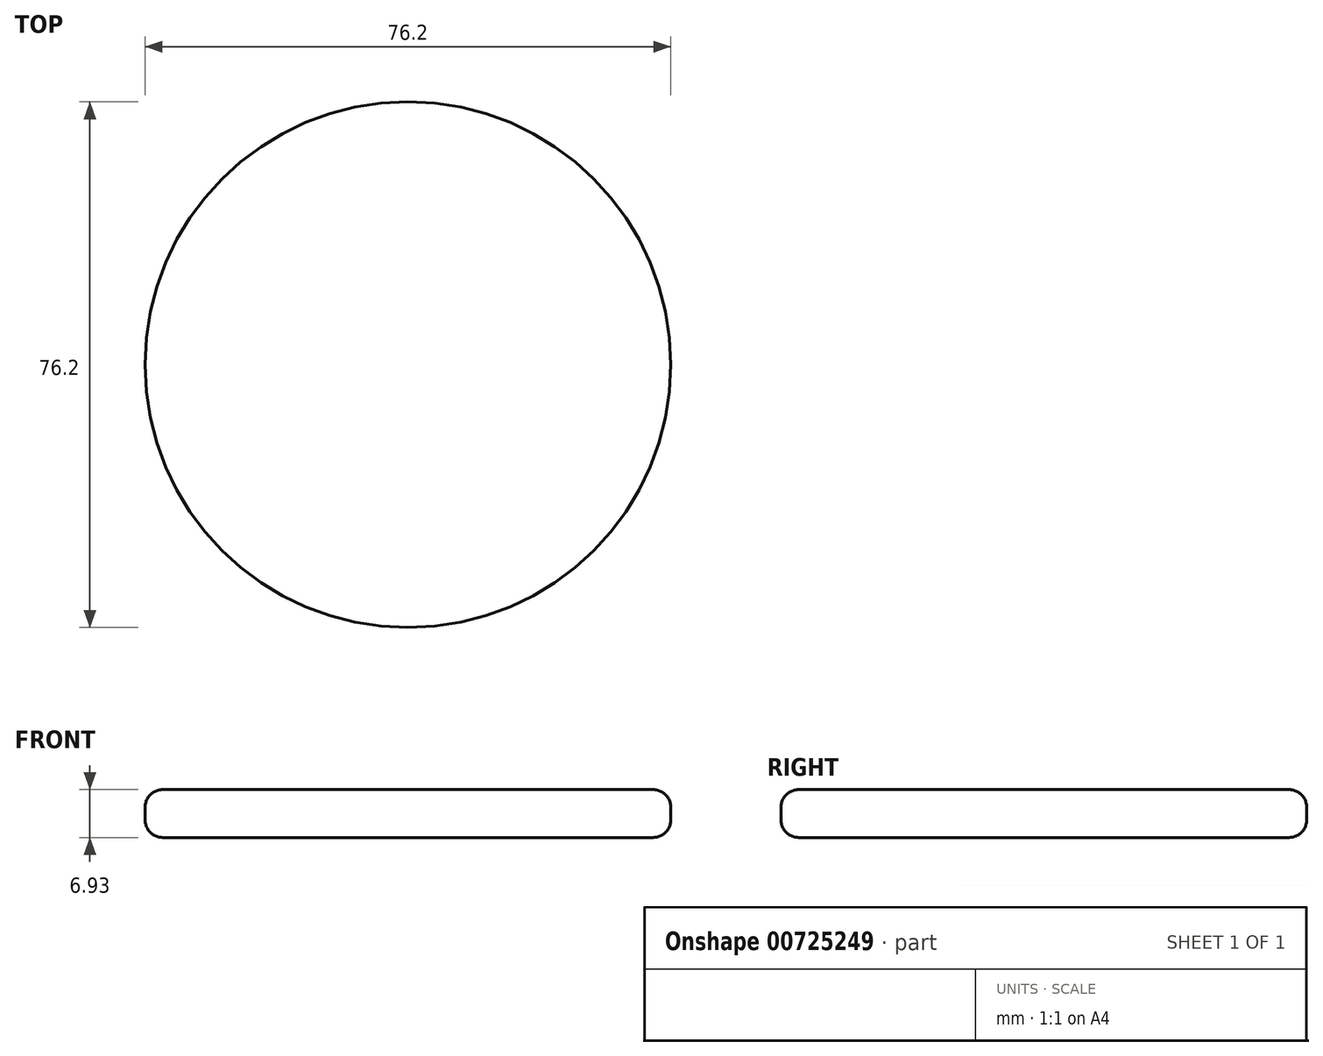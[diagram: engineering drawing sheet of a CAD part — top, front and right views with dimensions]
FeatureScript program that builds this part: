
annotation { "Feature Type Name" : "Feature", "Feature Type Description" : "" }
export const myFeature = defineFeature(function(context is Context, id is Id, definition is map)
    precondition{}
    {
        {
            var Q0;
            Q0=qCreatedBy(makeId("Top.planeOp"),FACE);
            var sketch = newSketch(context, id + "F0", { "sketchPlane" : qUnion([Q0])});
            skCircle(sketch, "E0", {"center": v(0, 0) * mm, "radius": 38.1 * mm});
            skSolve(sketch);
        }
        {
            var Q0;
            Q0 = qSketchRegion(id + "F0", true);
            extrude(context, id + "F1", {"entities" : qUnion([Q0]), "depth" : 6.93 * mm, "offsetDistance" : 25.4 * mm});
        }
        {
            var Q0;
            Q0=makeQuery(id+"F1.opExtrude","CAP_EDGE",EDGE,{"disambiguationData":[OSD([sQuery(id+"F0.wireOp",EDGE,"E0")])],"isStart":false});
            fillet(context, id + "F2", {"entities" : qUnion([Q0]), "radius" : 2.54 * mm, "tangentPropagation" : true, "allowEdgeOverflow" : false});
        }
        {
            var Q0;
            Q0=makeQuery(id+"F1.opExtrude","CAP_EDGE",EDGE,{"disambiguationData":[OSD([sQuery(id+"F0.wireOp",EDGE,"E0")])],"isStart":true});
            fillet(context, id + "F3", {"entities" : qUnion([Q0]), "radius" : 2.54 * mm, "tangentPropagation" : true, "allowEdgeOverflow" : false});
        }
    });
